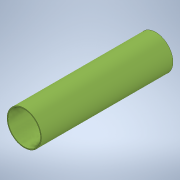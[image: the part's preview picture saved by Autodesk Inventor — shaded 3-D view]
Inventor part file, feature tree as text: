
AUTODESK INVENTOR PART (.ipt)
format: ipt  version: 2020 (Build 240168000, 168)  size: 97,280 bytes
history: native  units: mm
features: extrude x1, sketch x1
ambient origin geometry x8: Origin, YZ Plane, XZ Plane, XY Plane, X Axis, Y Axis, Z Axis, Center Point
bodies: Solid1 (feature_tree)
feature tree (2):
  extrude  "Extrusion1"  Depth=210.0mm
  sketch  "Sketch1"  dims[d0=55.0mm d1=52.0mm d2=210.0mm d3=0.0mm]
